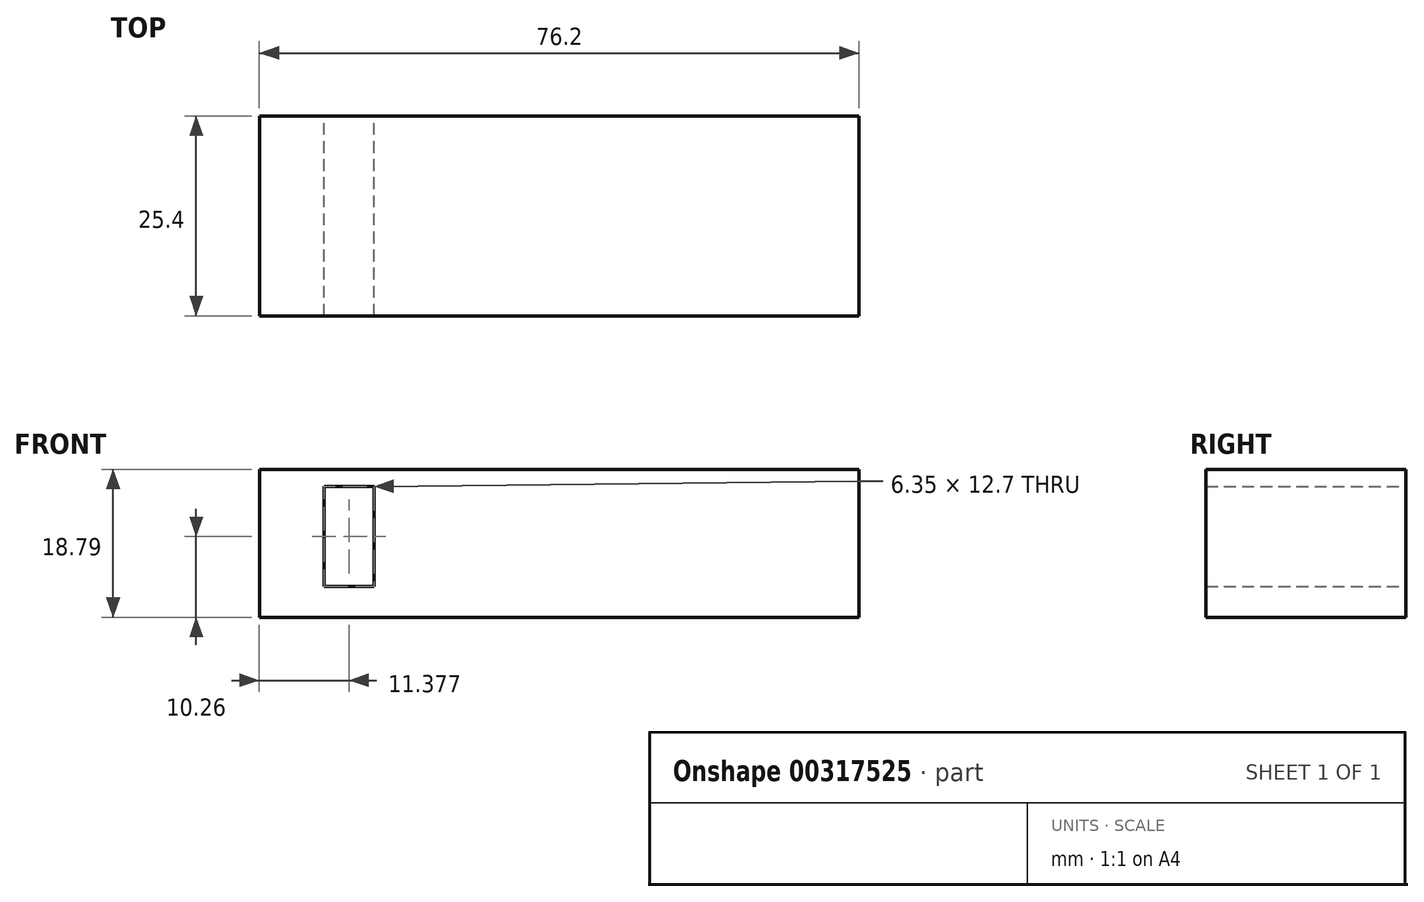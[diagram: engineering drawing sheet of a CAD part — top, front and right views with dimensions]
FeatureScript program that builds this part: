
annotation { "Feature Type Name" : "Feature", "Feature Type Description" : "" }
export const myFeature = defineFeature(function(context is Context, id is Id, definition is map)
    precondition{}
    {
        {
            var Q0;
            Q0=qCreatedBy(makeId("Front.planeOp"),FACE);
            var sketch = newSketch(context, id + "F0", { "sketchPlane" : qUnion([Q0])});
            skLineSegment(sketch, "E0.bottom", {"start": v(-25.88, 22.15) * mm, "end": v(50.32, 22.15) * mm});
            skLineSegment(sketch, "E0.top", {"start": v(-25.88, 40.94) * mm, "end": v(50.32, 40.94) * mm});
            skLineSegment(sketch, "E0.left", {"start": v(-25.88, 22.15) * mm, "end": v(-25.88, 40.94) * mm});
            skLineSegment(sketch, "E0.right", {"start": v(50.32, 22.15) * mm, "end": v(50.32, 40.94) * mm});
            skLineSegment(sketch, "E1.bottom", {"start": v(-17.68, 38.76) * mm, "end": v(-11.33, 38.76) * mm});
            skLineSegment(sketch, "E1.top", {"start": v(-17.68, 26.06) * mm, "end": v(-11.33, 26.06) * mm});
            skLineSegment(sketch, "E1.left", {"start": v(-17.68, 38.76) * mm, "end": v(-17.68, 26.06) * mm});
            skLineSegment(sketch, "E1.right", {"start": v(-11.33, 38.76) * mm, "end": v(-11.33, 26.06) * mm});
            skSolve(sketch);
        }
        {
            var Q0;
            Q0=makeQuery(id+"F0.imprint","IMPRINT",FACE,{"disambiguationData":[TD([[makeQuery(id+"F0.imprint","IMPRINT",EDGE,{"derivedFrom":sQuery(id+"F0.wireOp",EDGE,"E0.bottom")}),1.0]])]});
            extrude(context, id + "F1", {"entities" : qUnion([Q0]), "depth" : 25.4 * mm});
        }
    });
